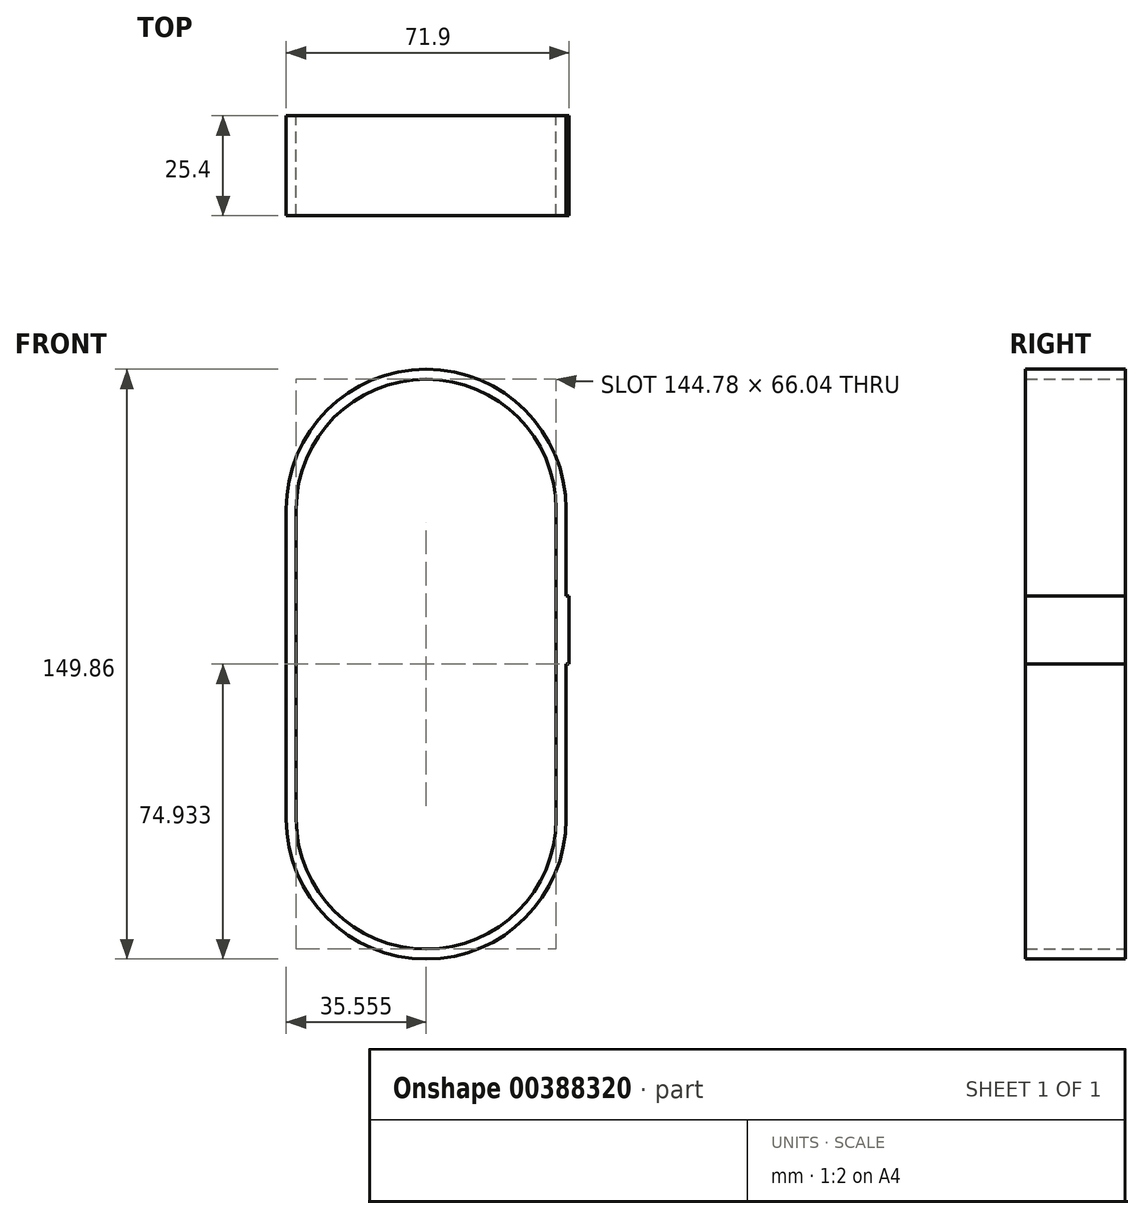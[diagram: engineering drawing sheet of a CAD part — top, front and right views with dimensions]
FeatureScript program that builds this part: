
annotation { "Feature Type Name" : "Feature", "Feature Type Description" : "" }
export const myFeature = defineFeature(function(context is Context, id is Id, definition is map)
    precondition{}
    {
        {
            var Q0;
            Q0=qCreatedBy(makeId("Front.planeOp"),FACE);
            var sketch = newSketch(context, id + "F0", { "sketchPlane" : qUnion([Q0])});
            skLineSegment(sketch, "E0", {"start": v(-54.07, 22) * mm, "end": v(-54.07, -56.74) * mm});
            skLineSegment(sketch, "E1", {"start": v(17.05, 22) * mm, "end": v(17.05, -56.74) * mm});
            skArc(sketch, "E2", {"start": v(17.05, 22) * mm, "mid": v(-18.51, 57.56) * mm, "end": v(-54.07, 22) * mm});
            skArc(sketch, "E3", {"start": v(-54.07, -56.74) * mm, "mid": v(-18.51, -92.3) * mm, "end": v(17.05, -56.74) * mm});
            skSolve(sketch);
        }
        {
            var Q0;
            Q0=makeQuery(id+"F0.imprint","IMPRINT",FACE,{"disambiguationData":[TD([[makeQuery(id+"F0.imprint","IMPRINT",EDGE,{"derivedFrom":sQuery(id+"F0.wireOp",EDGE,"E0")}),1.0]])]});
            extrude(context, id + "F1", {"entities" : qUnion([Q0]), "depth" : 25.4 * mm});
        }
        {
            var Q0;
            Q0=makeQuery(id+"F1.opExtrude","CAP_FACE",FACE,{"disambiguationData":[OSD([sQuery(id+"F0.wireOp",EDGE,"E0"),sQuery(id+"F0.wireOp",EDGE,"E1"),sQuery(id+"F0.wireOp",EDGE,"E2"),sQuery(id+"F0.wireOp",EDGE,"E3")])],"isStart":false});
            var Q1;
            Q1=makeQuery(id+"F1.opExtrude","CAP_FACE",FACE,{"disambiguationData":[OSD([sQuery(id+"F0.wireOp",EDGE,"E0"),sQuery(id+"F0.wireOp",EDGE,"E1"),sQuery(id+"F0.wireOp",EDGE,"E2"),sQuery(id+"F0.wireOp",EDGE,"E3")])],"isStart":true});
            shell(context, id + "F2", {"entities" : qUnion([Q0, Q1]), "thickness" : 2.54 * mm});
        }
        {
            var Q0;
            Q0=makeQuery(id+"F1.opExtrude","SWEPT_FACE",FACE,{"disambiguationData":[OSD([sQuery(id+"F0.wireOp",EDGE,"E1")])]});
            var sketch = newSketch(context, id + "F3", { "sketchPlane" : qUnion([Q0])});
            skLineSegment(sketch, "E4", {"start": v(-25.4, 0) * mm, "end": v(0, 0) * mm});
            skLineSegment(sketch, "E5", {"start": v(-25.4, -17.37) * mm, "end": v(0, -17.37) * mm});
            skLineSegment(sketch, "E6", {"start": v(0, -17.37) * mm, "end": v(0, 0) * mm});
            skLineSegment(sketch, "E7", {"start": v(-25.4, 0) * mm, "end": v(-25.4, -17.37) * mm});
            skSolve(sketch);
        }
        {
            var Q0;
            Q0 = qSketchRegion(id + "F3", true);
            extrude(context, id + "F4", {"entities" : qUnion([Q0]), "operationType" : NewBodyOperationType.ADD, "depth" : 0.79 * mm});
        }
    });
